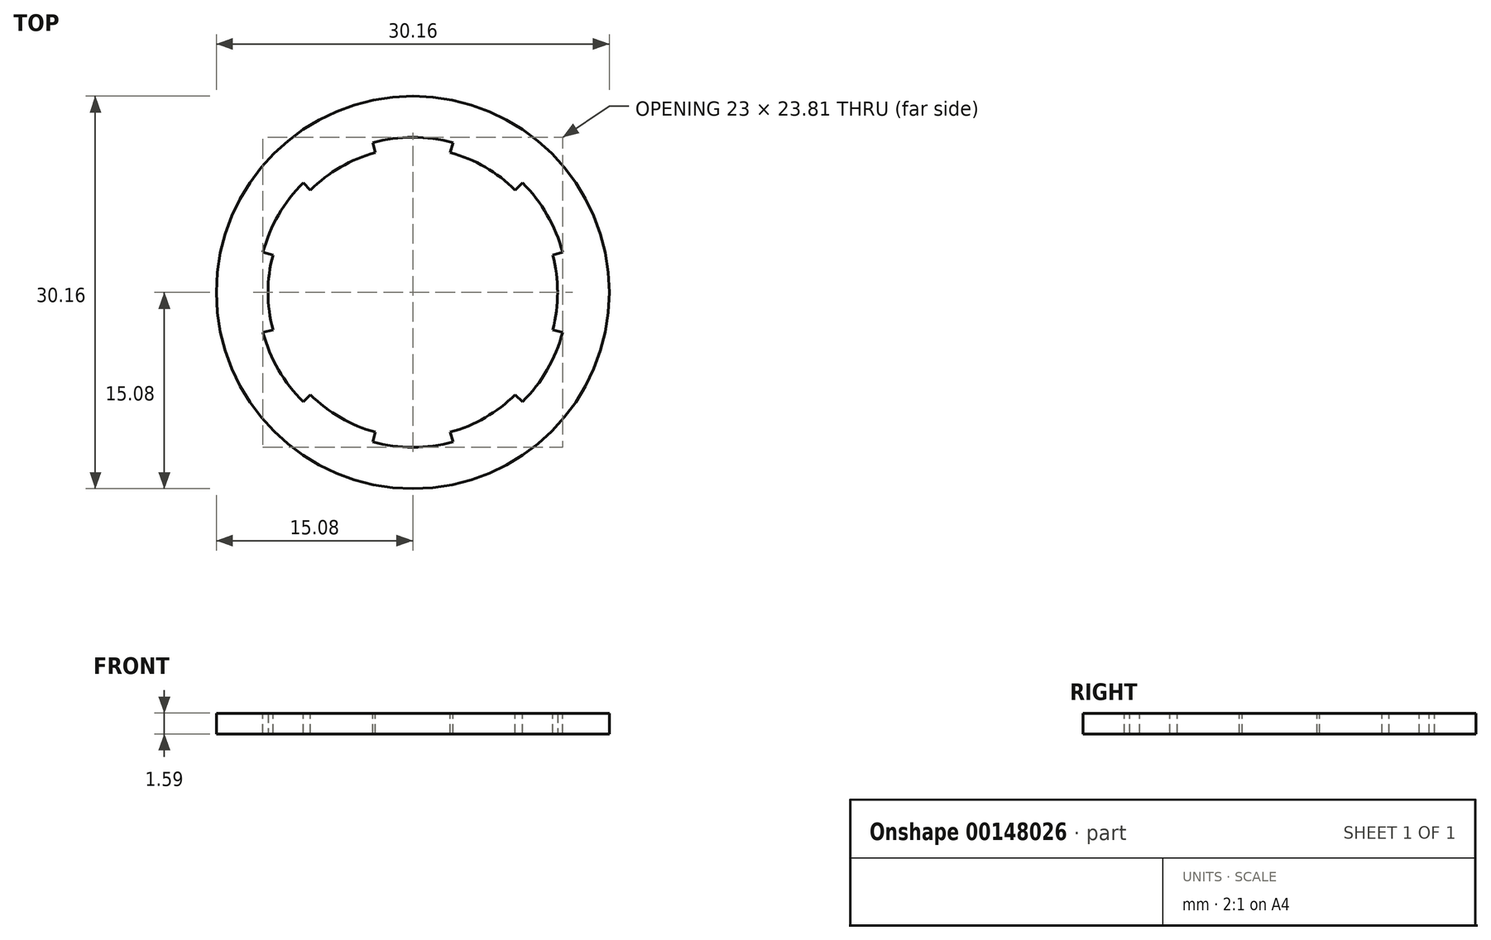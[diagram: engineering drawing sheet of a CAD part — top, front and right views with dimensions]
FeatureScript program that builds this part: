
annotation { "Feature Type Name" : "Feature", "Feature Type Description" : "" }
export const myFeature = defineFeature(function(context is Context, id is Id, definition is map)
    precondition{}
    {
        {
            var Q0;
            Q0=qCreatedBy(makeId("Top.planeOp"),FACE);
            var sketch = newSketch(context, id + "F0", { "sketchPlane" : qUnion([Q0])});
            skCircle(sketch, "E0", {"center": v(0, 0) * mm, "radius": 15.08 * mm});
            skCircle(sketch, "E1", {"center": v(0, 0) * mm, "radius": 11.11 * mm});
            skCircle(sketch, "E2", {"center": v(0, 0) * mm, "radius": 11.9 * mm, "construction": true});
            skSolve(sketch);
        }
        {
            var Q0;
            Q0=qSketchRegion(id+"F0",true);
            extrude(context, id + "F1", {"entities" : qUnion([Q0]), "depth" : 1.59 * mm});
        }
        {
            var Q0;
            Q0=makeQuery(id+"F1.opExtrude","CAP_FACE",FACE,{"disambiguationData":[OSD([sQuery(id+"F0.wireOp",EDGE,"E0"),sQuery(id+"F0.wireOp",EDGE,"E1")])],"isStart":false});
            var sketch = newSketch(context, id + "F2", { "sketchPlane" : qUnion([Q0])});
            skLineSegment(sketch, "E3", {"start": v(0, 0) * mm, "end": v(0, 11.11) * mm, "construction": true});
            skArc(sketch, "E4", {"start": v(2.88, 10.73) * mm, "mid": v(0, 11.11) * mm, "end": v(-2.88, 10.73) * mm});
            skLineSegment(sketch, "E5", {"start": v(-2.88, 10.73) * mm, "end": v(-3.08, 11.5) * mm});
            skLineSegment(sketch, "E6", {"start": v(2.88, 10.73) * mm, "end": v(3.08, 11.5) * mm});
            skLineSegment(sketch, "E7", {"start": v(0, 0) * mm, "end": v(-2.88, 10.73) * mm, "construction": true});
            skLineSegment(sketch, "E8", {"start": v(0, 0) * mm, "end": v(2.88, 10.73) * mm, "construction": true});
            skArc(sketch, "E9", {"start": v(3.08, 11.5) * mm, "mid": v(0, 11.9) * mm, "end": v(-3.08, 11.5) * mm});
            skSolve(sketch);
        }
        {
            var Q0;
            Q0=qSketchRegion(id+"F2",true);
            var Q1;
            Q1=makeQuery(id+"F1.opExtrude","CAP_FACE",FACE,{"disambiguationData":[OSD([sQuery(id+"F0.wireOp",EDGE,"E0"),sQuery(id+"F0.wireOp",EDGE,"E1")])],"isStart":true});
            extrude(context, id + "F3", {"entities" : qUnion([Q0]), "operationType" : NewBodyOperationType.REMOVE, "endBound" : BoundingType.UP_TO_SURFACE, "oppositeDirection" : true, "endBoundEntityFace" : qUnion([Q1]), "depth" : 25.4 * mm});
        }
        {
            var Q0;
            Q0=makeQuery(id+"F3.boolean.opBoolean","COPY",FACE,{"derivedFrom":makeQuery(id+"F3.opExtrude","SWEPT_FACE",FACE,{"disambiguationData":[OSD([sQuery(id+"F2.wireOp",EDGE,"E5")])]})});
            var Q1;
            Q1=makeQuery(id+"F3.boolean.opBoolean","COPY",FACE,{"derivedFrom":makeQuery(id+"F3.opExtrude","SWEPT_FACE",FACE,{"disambiguationData":[OSD([sQuery(id+"F2.wireOp",EDGE,"E9")])]})});
            var Q2;
            Q2=makeQuery(id+"F3.boolean.opBoolean","COPY",FACE,{"derivedFrom":makeQuery(id+"F3.opExtrude","SWEPT_FACE",FACE,{"disambiguationData":[OSD([sQuery(id+"F2.wireOp",EDGE,"E6")])]})});
            var Q3;
            Q3=makeQuery(id+"F1.opExtrude","SWEPT_FACE",FACE,{"disambiguationData":[OSD([sQuery(id+"F0.wireOp",EDGE,"E1")])]});
            circularPattern(context, id + "F4", {"patternType" : PatternType.FACE, "faces" : qUnion([Q0, Q1, Q2]), "axis" : qUnion([Q3]), "angle" : 60 * degree, "instanceCount" : 6});
        }
    });
